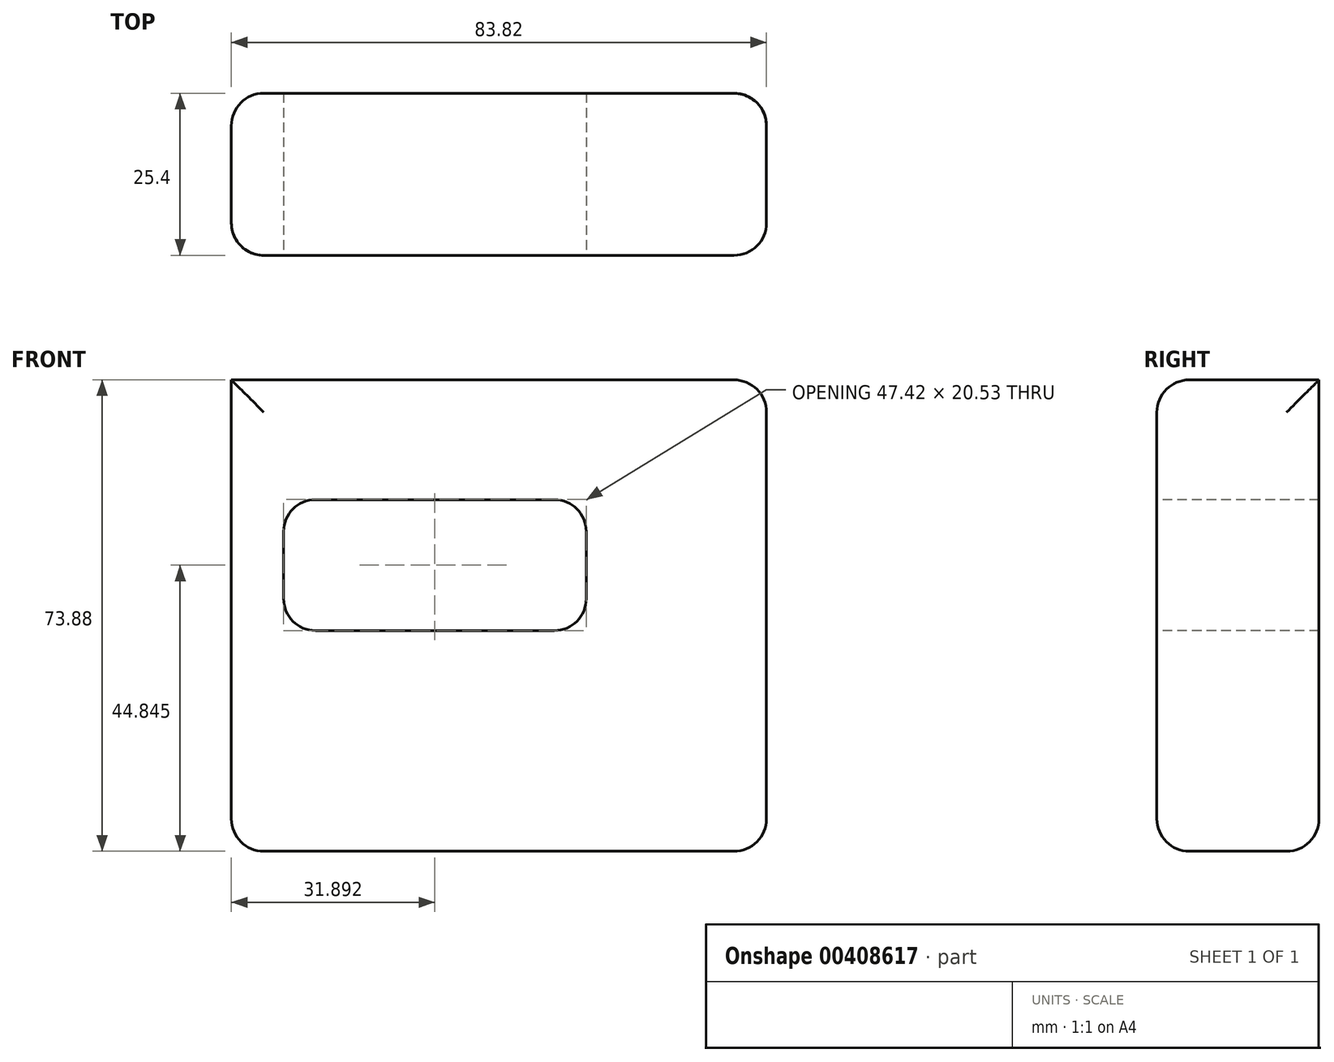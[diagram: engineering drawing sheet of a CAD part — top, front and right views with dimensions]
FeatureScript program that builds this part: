
annotation { "Feature Type Name" : "Feature", "Feature Type Description" : "" }
export const myFeature = defineFeature(function(context is Context, id is Id, definition is map)
    precondition{}
    {
        {
            var Q0;
            Q0=qCreatedBy(makeId("Front.planeOp"),FACE);
            var sketch = newSketch(context, id + "F0", { "sketchPlane" : qUnion([Q0])});
            skLineSegment(sketch, "E0.bottom", {"start": v(-55.6, 55.92) * mm, "end": v(28.22, 55.92) * mm});
            skLineSegment(sketch, "E0.top", {"start": v(-55.6, -17.96) * mm, "end": v(28.22, -17.96) * mm});
            skLineSegment(sketch, "E0.left", {"start": v(-55.6, 55.92) * mm, "end": v(-55.6, -17.96) * mm});
            skLineSegment(sketch, "E0.right", {"start": v(28.22, 55.92) * mm, "end": v(28.22, -17.96) * mm});
            skSolve(sketch);
        }
        {
            var Q0;
            Q0 = qSketchRegion(id + "FemGLsqiH4PDFwr_0", true);
            var Q1;
            Q1=makeQuery(id+"F0.imprint","IMPRINT",FACE,{"disambiguationData":[TD([[makeQuery(id+"F0.imprint","IMPRINT",EDGE,{"derivedFrom":sQuery(id+"F0.wireOp",EDGE,"E0.bottom")}),-1.0]])]});
            extrude(context, id + "F1", {"entities" : qUnion([Q0, Q1]), "depth" : 25.4 * mm});
        }
        {
            var Q0;
            Q0=makeQuery(id+"F1.opExtrude","CAP_FACE",FACE,{"disambiguationData":[OSD([sQuery(id+"F0.wireOp",EDGE,"E0.bottom"),sQuery(id+"F0.wireOp",EDGE,"E0.top"),sQuery(id+"F0.wireOp",EDGE,"E0.left"),sQuery(id+"F0.wireOp",EDGE,"E0.right")])],"isStart":false});
            var sketch = newSketch(context, id + "F2", { "sketchPlane" : qUnion([Q0])});
            skLineSegment(sketch, "E1.bottom", {"start": v(-5, 37.15) * mm, "end": v(-42.42, 37.15) * mm});
            skLineSegment(sketch, "E1.top", {"start": v(-5, 16.62) * mm, "end": v(-42.42, 16.62) * mm});
            skLineSegment(sketch, "E1.left", {"start": v(0, 32.15) * mm, "end": v(0, 21.62) * mm});
            skLineSegment(sketch, "E1.right", {"start": v(-47.42, 32.15) * mm, "end": v(-47.42, 21.62) * mm});
            skPoint(sketch, "E1.middle", {"position": v(-23.7, 26.89) * mm});
            skPoint(sketch, "E2.visualSharp", {"position": v(0, 37.15) * mm});
            skArc(sketch, "E2.filletArc", {"start": v(0, 32.15) * mm, "mid": v(-1.46, 35.69) * mm, "end": v(-5, 37.15) * mm});
            skPoint(sketch, "E3.visualSharp", {"position": v(-47.42, 37.15) * mm});
            skArc(sketch, "E3.filletArc", {"start": v(-42.42, 37.15) * mm, "mid": v(-45.95, 35.69) * mm, "end": v(-47.42, 32.15) * mm});
            skPoint(sketch, "E4.visualSharp", {"position": v(0, 16.62) * mm});
            skArc(sketch, "E4.filletArc", {"start": v(-5, 16.62) * mm, "mid": v(-1.46, 18.08) * mm, "end": v(0, 21.62) * mm});
            skPoint(sketch, "E5.visualSharp", {"position": v(-47.42, 16.62) * mm});
            skArc(sketch, "E5.filletArc", {"start": v(-47.42, 21.62) * mm, "mid": v(-45.95, 18.08) * mm, "end": v(-42.42, 16.62) * mm});
            skSolve(sketch);
        }
        {
            var Q0;
            Q0=makeQuery(id+"F2.imprint","IMPRINT",FACE,{"disambiguationData":[TD([[makeQuery(id+"F2.imprint","IMPRINT",EDGE,{"derivedFrom":sQuery(id+"F2.wireOp",EDGE,"E1.bottom")}),1.0]])]});
            extrude(context, id + "F3", {"entities" : qUnion([Q0]), "operationType" : NewBodyOperationType.REMOVE, "oppositeDirection" : true, "depth" : 25.4 * mm});
        }
        {
            var Q0;
            Q0=makeQuery(id+"F1.opExtrude","CAP_EDGE",EDGE,{"disambiguationData":[OSD([sQuery(id+"F0.wireOp",EDGE,"E0.right")])],"isStart":true});
            var Q1;
            Q1=makeQuery(id+"F1.opExtrude","SWEPT_EDGE",EDGE,{"disambiguationData":[OSD([sQuery(id+"F0.wireOp",EDGE,"E0.bottom"),sQuery(id+"F0.wireOp",EDGE,"E0.right")])]});
            fillet(context, id + "F4", {"entities" : qUnion([Q0, Q1]), "radius" : 5.08 * mm, "tangentPropagation" : true, "allowEdgeOverflow" : false});
        }
        {
            var Q0;
            Q0=makeQuery(id+"F1.opExtrude","CAP_EDGE",EDGE,{"disambiguationData":[OSD([sQuery(id+"F0.wireOp",EDGE,"E0.right")])],"isStart":false});
            var Q1;
            Q1=makeQuery(id+"F1.opExtrude","CAP_EDGE",EDGE,{"disambiguationData":[OSD([sQuery(id+"F0.wireOp",EDGE,"E0.top")])],"isStart":false});
            var Q2;
            Q2=makeQuery(id+"F1.opExtrude","CAP_EDGE",EDGE,{"disambiguationData":[OSD([sQuery(id+"F0.wireOp",EDGE,"E0.left")])],"isStart":false});
            var Q3;
            Q3=makeQuery(id+"F3.boolean.opBoolean","COPY",EDGE,{"derivedFrom":makeQuery(id+"F3.opExtrude","CAP_EDGE",EDGE,{"disambiguationData":[OSD([sQuery(id+"F2.wireOp",EDGE,"E1.bottom")])],"isStart":true})});
            var Q4;
            Q4=makeQuery(id+"F3.boolean.opBoolean","COPY",EDGE,{"derivedFrom":makeQuery(id+"F3.opExtrude","CAP_EDGE",EDGE,{"disambiguationData":[OSD([sQuery(id+"F2.wireOp",EDGE,"E2.filletArc")])],"isStart":true})});
            var Q5;
            Q5=makeQuery(id+"F1.opExtrude","SWEPT_EDGE",EDGE,{"disambiguationData":[OSD([sQuery(id+"F0.wireOp",EDGE,"E0.top"),sQuery(id+"F0.wireOp",EDGE,"E0.left")])]});
            var Q6;
            Q6=makeQuery(id+"F1.opExtrude","CAP_EDGE",EDGE,{"disambiguationData":[OSD([sQuery(id+"F0.wireOp",EDGE,"E0.left")])],"isStart":true});
            var Q7;
            Q7=makeQuery(id+"F1.opExtrude","CAP_EDGE",EDGE,{"disambiguationData":[OSD([sQuery(id+"F0.wireOp",EDGE,"E0.top")])],"isStart":true});
            var Q8;
            Q8=makeQuery(id+"F3.boolean.opBoolean","COPY",EDGE,{"derivedFrom":makeQuery(id+"F3.opExtrude","CAP_EDGE",EDGE,{"disambiguationData":[OSD([sQuery(id+"F2.wireOp",EDGE,"E1.top")])],"isStart":false})});
            var Q9;
            Q9=makeQuery(id+"F3.boolean.opBoolean","COPY",EDGE,{"derivedFrom":makeQuery(id+"F3.opExtrude","CAP_EDGE",EDGE,{"disambiguationData":[OSD([sQuery(id+"F2.wireOp",EDGE,"E5.filletArc")])],"isStart":false})});
            fillet(context, id + "F5", {"entities" : qUnion([Q0, Q1, Q2, Q3, Q4, Q5, Q6, Q7, Q8, Q9]), "radius" : 5.08 * mm, "tangentPropagation" : true, "allowEdgeOverflow" : false});
        }
    });
